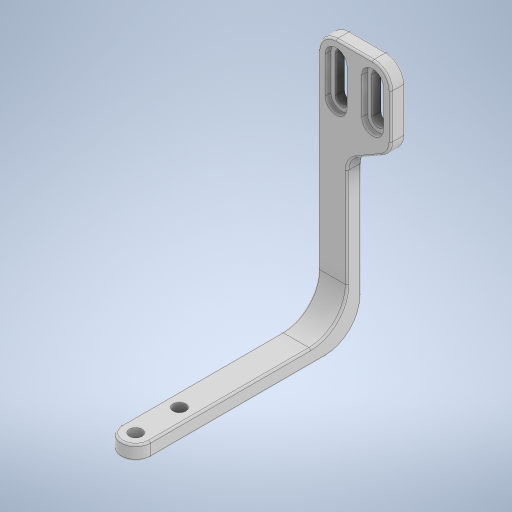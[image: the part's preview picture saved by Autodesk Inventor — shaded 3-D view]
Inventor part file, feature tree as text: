
AUTODESK INVENTOR PART (.ipt)
format: ipt  version: 2024.2 (Build 282272000, 272)  size: 414,720 bytes
history: native  units: mm
features: sketch x7, extrude x6, fillet x4, projected_geometry x2
ambient origin geometry x8: Origin, YZ Plane, XZ Plane, XY Plane, X Axis, Y Axis, Z Axis, Center Point
bodies: Solid1 (feature_tree)
feature tree (19):
  extrude  "Extrusion1"  Depth=10.0mm
  fillet  "Fillet1"  Radius=62.0mm
  extrude  "Extrusion5"  Depth=4.0mm
  extrude  "Extrusion2"  Depth=10.0mm
  extrude  "Extrusion3"  Depth=10.0mm
  extrude  "Extrusion4"  Depth=10.0mm
  fillet  "Fillet2"  Radius=1.5mm
  fillet  "Fillet3"  Radius=1.75mm
  fillet  "Fillet4"  Radius=1.75mm
  extrude  "Extrusion6"  Depth=12.0mm
  sketch  "Sketch8"  dims[d21=3.5mm d26=0.0mm d27=0.0mm d29=4.0mm d30=4.0mm d31=20.0mm d32=20.0mm d33=60.0deg d34=8.0mm d35=0.0mm d36=4.0mm d37=5.0mm d38=0.5mm d39=5.7mm d40=1.5mm d41=0.0mm]
  sketch  "Sketch1"  dims[d0=10.0mm d2=57.0mm d3=62.0mm]
  sketch  "Sketch3"  dims[d4=4.0mm d5=4.0mm]
  sketch  "Sketch4"  dims[d6=8.0mm d7=0.0mm d8=10.0mm]
  projected_geometry  "Projected Loop1"
  projected_geometry  "Projected Loop2"
  sketch  "Sketch5"  dims[d10=3.0mm d11=10.0mm]
  sketch  "Sketch6"  dims[d12=5.0mm d13=10.0mm d14=1.5mm d15=0.0mm d16=1.75mm d17=1.75mm]
  sketch  "Sketch7"  dims[d18=0.0mm d19=0.0mm d20=12.0mm]
